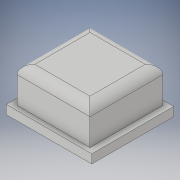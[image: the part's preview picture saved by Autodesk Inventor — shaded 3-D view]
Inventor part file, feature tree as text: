
AUTODESK INVENTOR PART (.ipt)
format: ipt  version: 2019 (Build 230136000, 136)  size: 138,240 bytes
history: native  units: mm
features: extrude x3, sketch x3, other x1, shell x1, fillet x1, chamfer x1
ambient origin geometry x8: Origin, YZ Plane, XZ Plane, XY Plane, X Axis, Y Axis, Z Axis, Center Point
bodies: Body1 (feature_tree)
feature tree (10):
  other  "Твердое тело1"
  extrude  "Выдавливание1"  Depth=8.2mm
  shell  "Оболочка1"  Thickness=5.0mm
  extrude  "Выдавливание2"  Depth=0.8mm
  fillet  "Сопряжение1"  Radius=1.0mm
  extrude  "Выдавливание4"  Depth=1.0mm
  chamfer  "Фаска1"  Distance=0.5mm
  sketch  "Эскиз1"
  sketch  "Эскиз3"
  sketch  "Эскиз5"
